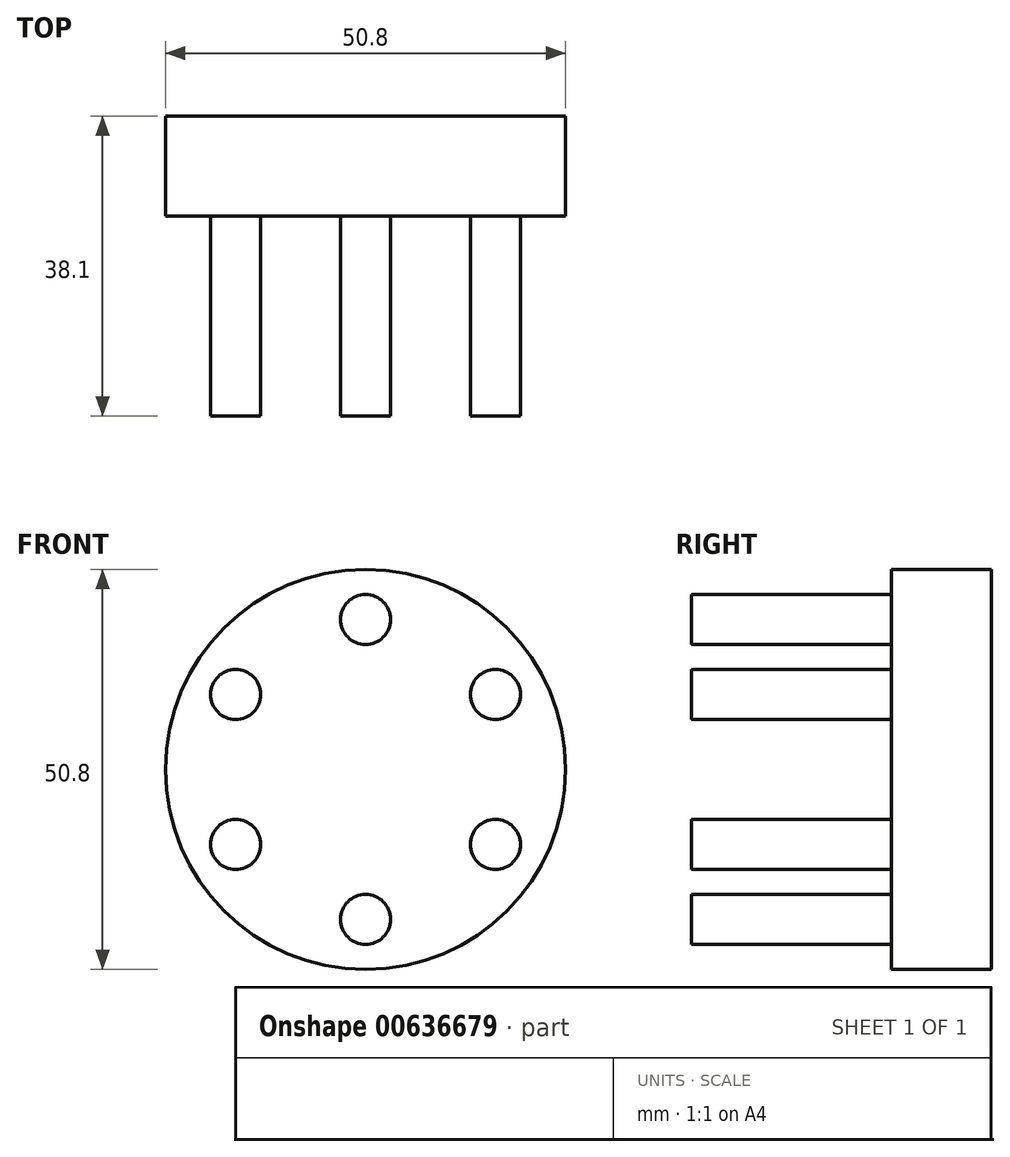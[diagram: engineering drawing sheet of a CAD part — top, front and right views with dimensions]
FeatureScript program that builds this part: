
annotation { "Feature Type Name" : "Feature", "Feature Type Description" : "" }
export const myFeature = defineFeature(function(context is Context, id is Id, definition is map)
    precondition{}
    {
        {
            var Q0;
            Q0=qCreatedBy(makeId("Front.planeOp"),FACE);
            var sketch = newSketch(context, id + "F0", { "sketchPlane" : qUnion([Q0])});
            skCircle(sketch, "E0", {"center": v(0, 0) * mm, "radius": 25.4 * mm});
            skSolve(sketch);
        }
        {
            var Q0;
            Q0 = qSketchRegion(id + "F0", true);
            extrude(context, id + "F1", {"entities" : qUnion([Q0]), "depth" : 12.7 * mm, "offsetDistance" : 25.4 * mm});
        }
        {
            var Q0;
            Q0=makeQuery(id+"F1.opExtrude","CAP_FACE",FACE,{"disambiguationData":[OSD([sQuery(id+"F0.wireOp",EDGE,"E0")])],"isStart":false});
            var sketch = newSketch(context, id + "F2", { "sketchPlane" : qUnion([Q0])});
            skLineSegment(sketch, "E1", {"start": v(0, 25.4) * mm, "end": v(0, 19.05) * mm, "construction": true});
            skCircle(sketch, "E2", {"center": v(0, 19.05) * mm, "radius": 3.18 * mm});
            skCircle(sketch, "E3.1.0", {"center": v(-16.5, 9.53) * mm, "radius": 3.18 * mm});
            skCircle(sketch, "E3.2.0", {"center": v(-16.5, -9.52) * mm, "radius": 3.18 * mm});
            skCircle(sketch, "E3.3.0", {"center": v(0, -19.05) * mm, "radius": 3.18 * mm});
            skCircle(sketch, "E3.4.0", {"center": v(16.5, -9.53) * mm, "radius": 3.18 * mm});
            skCircle(sketch, "E3.5.0", {"center": v(16.5, 9.53) * mm, "radius": 3.18 * mm});
            skPoint(sketch, "E3.center", {"position": v(0, 0) * mm});
            skSolve(sketch);
        }
        {
            var Q0;
            Q0 = qSketchRegion(id + "F2", true);
            extrude(context, id + "F3", {"entities" : qUnion([Q0]), "operationType" : NewBodyOperationType.ADD, "depth" : 25.4 * mm, "offsetDistance" : 25.4 * mm});
        }
    });
